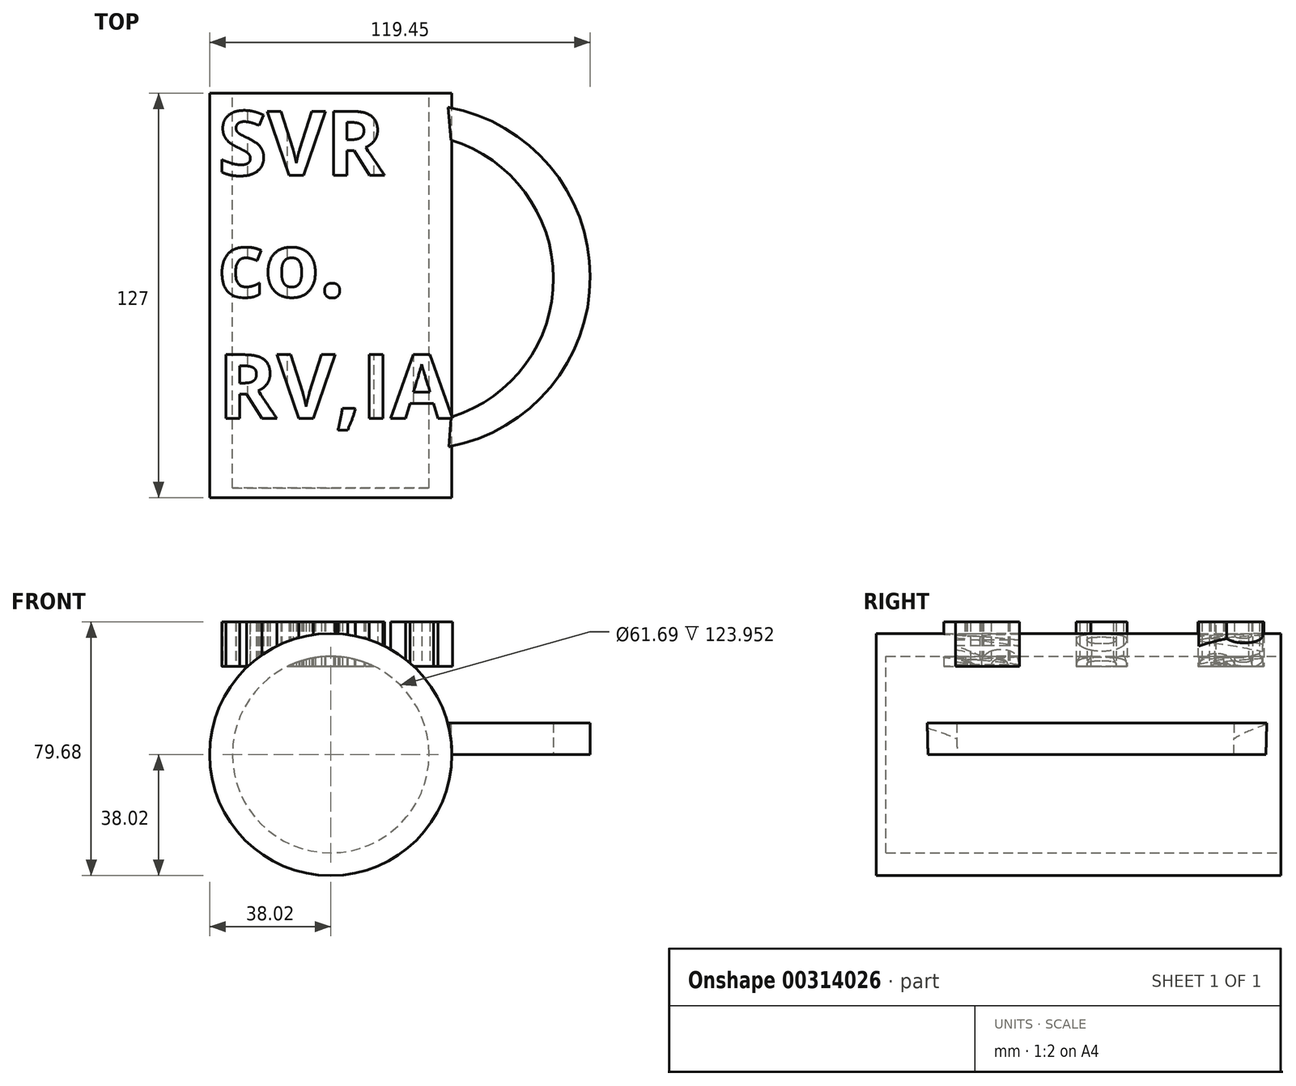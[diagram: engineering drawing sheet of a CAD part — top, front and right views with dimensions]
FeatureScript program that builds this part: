
annotation { "Feature Type Name" : "Feature", "Feature Type Description" : "" }
export const myFeature = defineFeature(function(context is Context, id is Id, definition is map)
    precondition{}
    {
        {
            var Q0;
            Q0=qCreatedBy(makeId("Front.planeOp"),FACE);
            var sketch = newSketch(context, id + "F0", { "sketchPlane" : qUnion([Q0])});
            skCircle(sketch, "E0", {"center": v(0, 0) * mm, "radius": 38.02 * mm});
            skSolve(sketch);
        }
        {
            var Q0;
            Q0 = qSketchRegion(id + "F0", true);
            extrude(context, id + "F1", {"entities" : qUnion([Q0]), "depth" : 127 * mm});
        }
        {
            var Q0;
            Q0=qCreatedBy(makeId("Front.planeOp"),FACE);
            var sketch = newSketch(context, id + "F2", { "sketchPlane" : qUnion([Q0])});
            skCircle(sketch, "E1", {"center": v(0, 0) * mm, "radius": 30.85 * mm});
            skSolve(sketch);
        }
        {
            var Q0;
            Q0 = qSketchRegion(id + "F2", true);
            extrude(context, id + "F3", {"entities" : qUnion([Q0]), "operationType" : NewBodyOperationType.REMOVE, "depth" : 123.95 * mm});
        }
        {
            var Q0;
            Q0=qCreatedBy(makeId("Top.planeOp"),FACE);
            var sketch = newSketch(context, id + "F4", { "sketchPlane" : qUnion([Q0])});
            skArc(sketch, "E2", {"start": v(37.7, -101.77) * mm, "mid": v(69.9, -58.24) * mm, "end": v(37.7, -14.71) * mm});
            skArc(sketch, "E3", {"start": v(37.1, -111) * mm, "mid": v(81.43, -57.6) * mm, "end": v(36.82, -4.44) * mm});
            skLineSegment(sketch, "E4", {"start": v(36.82, -4.44) * mm, "end": v(37.7, -14.71) * mm});
            skLineSegment(sketch, "E5", {"start": v(37.1, -111) * mm, "end": v(37.7, -101.77) * mm});
            skSolve(sketch);
        }
        {
            var Q0;
            Q0 = qSketchRegion(id + "F4", true);
            extrude(context, id + "F5", {"entities" : qUnion([Q0]), "operationType" : NewBodyOperationType.ADD, "depth" : 9.9 * mm});
        }
        {
            var Q0;
            Q0=qCreatedBy(makeId("Top.planeOp"),FACE);
            var sketch = newSketch(context, id + "F6", { "sketchPlane" : qUnion([Q0])});
            skText(sketch, "E6", { "text": "SVR\nco.\nRV,IA\n", "fontName": "OpenSans-Bold.ttf"});
            const initialGuessF6  = {"E6": [-0.0354, -0.02575, 1, 0, 0.02023]};
            skSetInitialGuess(sketch, initialGuessF6);
            skSolve(sketch);
        }
        {
            var Q0;
            Q0 = qSketchRegion(id + "F6", true);
            extrude(context, id + "F7", {"entities" : qUnion([Q0]), "operationType" : NewBodyOperationType.ADD, "depth" : 41.66 * mm, "hasSecondDirection" : true, "secondDirectionOppositeDirection" : false, "secondDirectionDepth" : 27.7 * mm});
        }
    });
